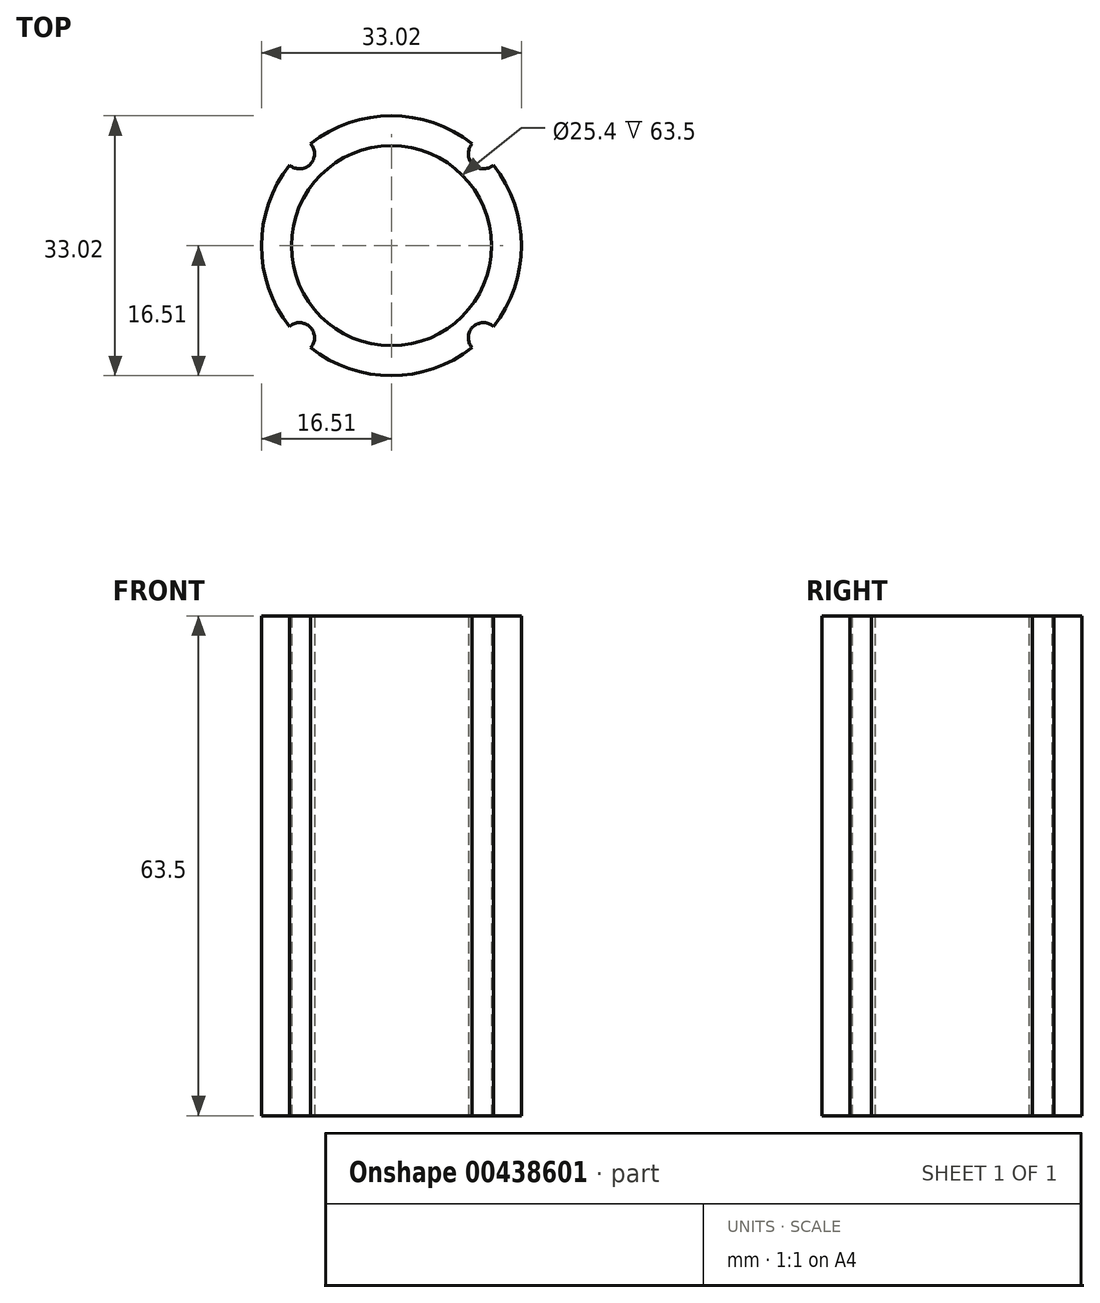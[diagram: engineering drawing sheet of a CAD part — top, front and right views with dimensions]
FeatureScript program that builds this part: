
annotation { "Feature Type Name" : "Feature", "Feature Type Description" : "" }
export const myFeature = defineFeature(function(context is Context, id is Id, definition is map)
    precondition{}
    {
        {
            var Q0;
            Q0=qCreatedBy(makeId("Top.planeOp"),FACE);
            var sketch = newSketch(context, id + "F0", { "sketchPlane" : qUnion([Q0])});
            skCircle(sketch, "E0", {"center": v(0, 0) * mm, "radius": 12.7 * mm});
            skPoint(sketch, "E1.0.midPoint", {"position": v(-12.7, 0) * mm});
            skCircle(sketch, "E2.0", {"center": v(0, 0) * mm, "radius": 16.51 * mm});
            skLineSegment(sketch, "E3.bottom", {"start": v(11.67, 11.67) * mm, "end": v(-11.67, 11.67) * mm, "construction": true});
            skLineSegment(sketch, "E3.top", {"start": v(11.67, -11.67) * mm, "end": v(-11.67, -11.67) * mm, "construction": true});
            skLineSegment(sketch, "E3.left", {"start": v(11.67, 11.67) * mm, "end": v(11.67, -11.67) * mm, "construction": true});
            skLineSegment(sketch, "E3.right", {"start": v(-11.67, 11.67) * mm, "end": v(-11.67, -11.67) * mm, "construction": true});
            skCircle(sketch, "E4.0", {"center": v(0, 0) * mm, "radius": 14.6 * mm, "construction": true});
            skCircle(sketch, "E5", {"center": v(-11.67, -11.67) * mm, "radius": 1.9 * mm});
            skCircle(sketch, "E6", {"center": v(11.67, -11.67) * mm, "radius": 1.9 * mm});
            skCircle(sketch, "E7", {"center": v(11.67, 11.67) * mm, "radius": 1.9 * mm});
            skCircle(sketch, "E8", {"center": v(-11.67, 11.67) * mm, "radius": 1.9 * mm});
            skSolve(sketch);
        }
        {
            var Q0;
            Q0=makeQuery(id+"F0.imprint","IMPRINT",FACE,{"disambiguationData":[TD([[makeQuery(id+"F0.imprint","IMPRINT",EDGE,{"derivedFrom":sQuery(id+"F0.wireOp",EDGE,"E0")}),-1.0]])]});
            extrude(context, id + "F1", {"entities" : qUnion([Q0]), "depth" : 63.5 * mm});
        }
    });
